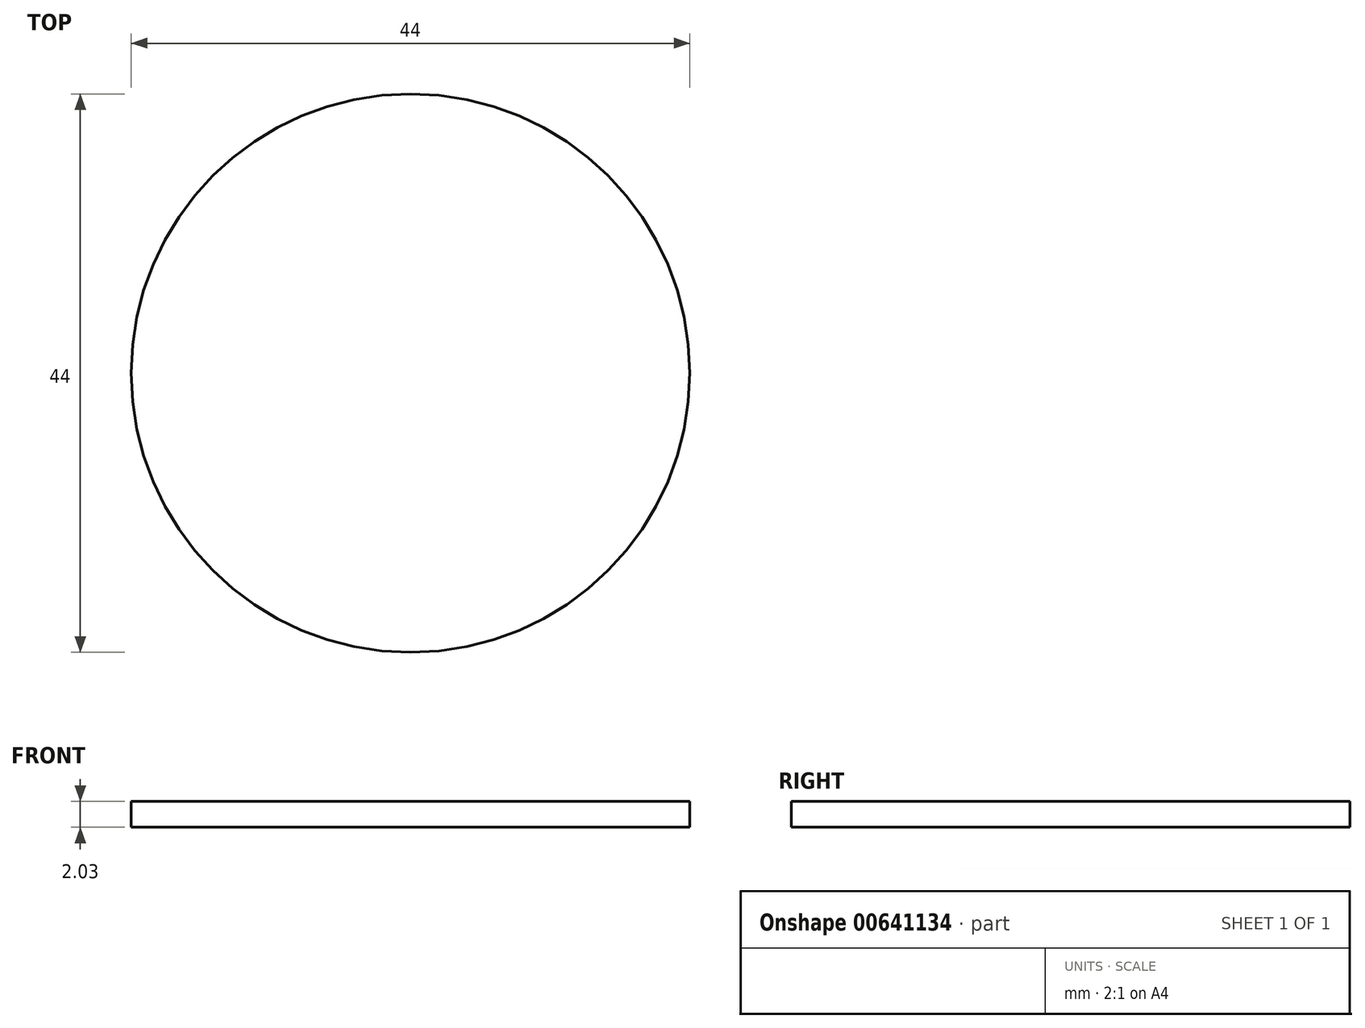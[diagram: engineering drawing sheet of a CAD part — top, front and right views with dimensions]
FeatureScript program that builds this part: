
annotation { "Feature Type Name" : "Feature", "Feature Type Description" : "" }
export const myFeature = defineFeature(function(context is Context, id is Id, definition is map)
    precondition{}
    {
        {
            var Q0;
            Q0=qCreatedBy(makeId("Top.planeOp"),FACE);
            var sketch = newSketch(context, id + "F0", { "sketchPlane" : qUnion([Q0])});
            skCircle(sketch, "E0", {"center": v(0, 0) * mm, "radius": 22 * mm});
            skSolve(sketch);
        }
        {
            var Q0;
            Q0=makeQuery(id+"F0.imprint","IMPRINT",FACE,{"disambiguationData":[TD([[makeQuery(id+"F0.imprint","IMPRINT",EDGE,{"derivedFrom":sQuery(id+"F0.wireOp",EDGE,"E0")}),1.0]])]});
            extrude(context, id + "F1", {"entities" : qUnion([Q0]), "depth" : 2.03 * mm, "offsetDistance" : 25.4 * mm});
        }
    });
